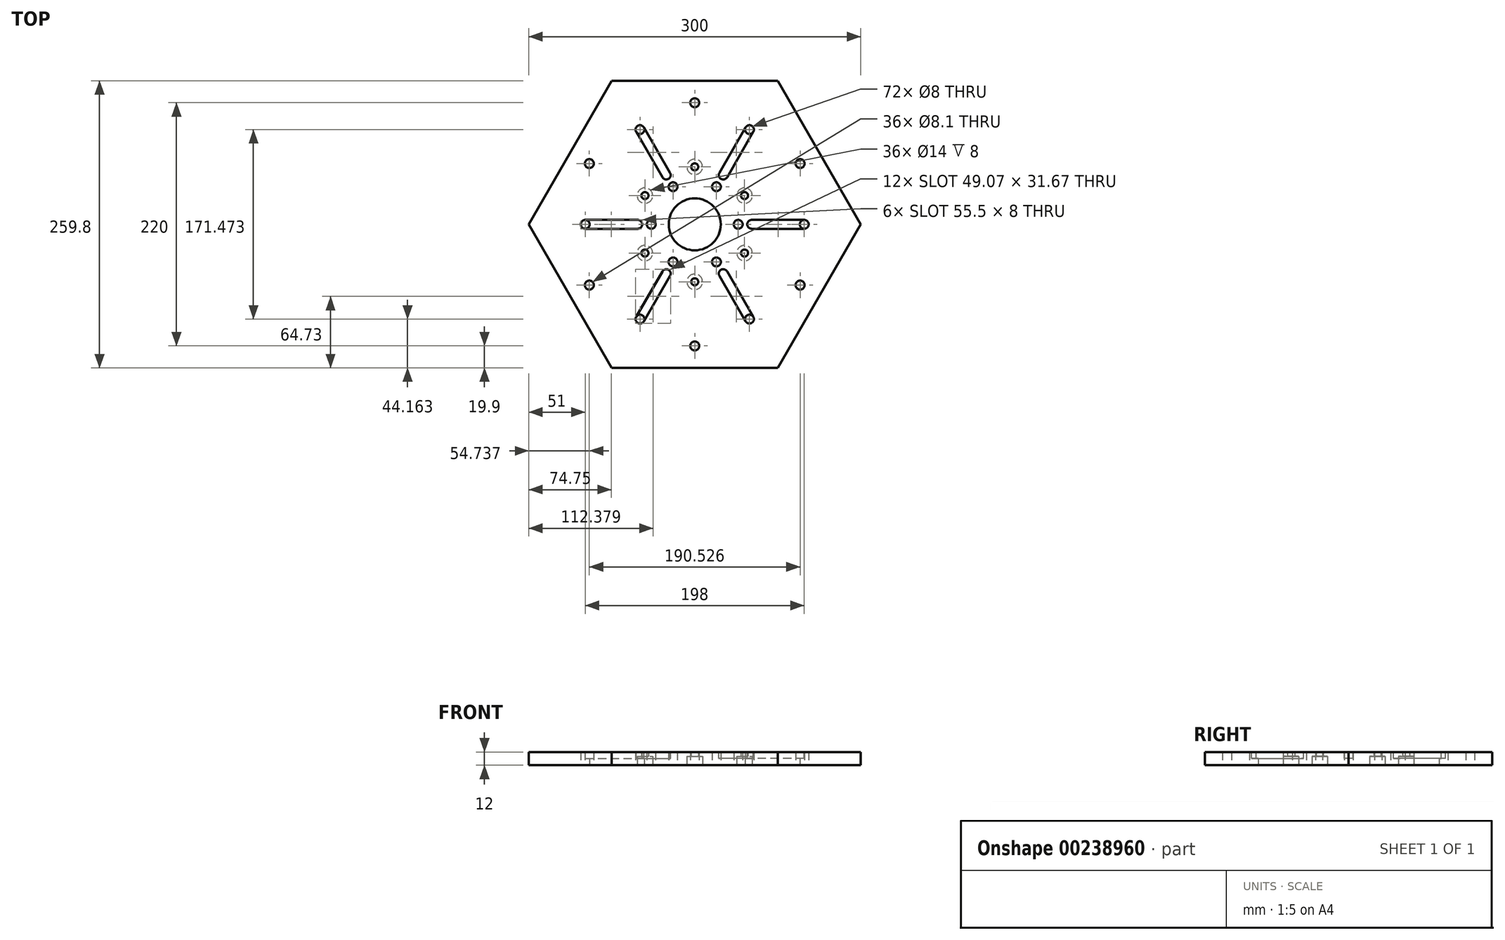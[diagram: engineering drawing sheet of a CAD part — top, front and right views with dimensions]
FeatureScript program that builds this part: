
annotation { "Feature Type Name" : "Feature", "Feature Type Description" : "" }
export const myFeature = defineFeature(function(context is Context, id is Id, definition is map)
    precondition{}
    {
        {
            var Q0;
            Q0=qCreatedBy(makeId("Top.planeOp"),FACE);
            var sketch = newSketch(context, id + "F0", { "sketchPlane" : qUnion([Q0])});
            skCircle(sketch, "E0.cCircle", {"center": v(0, 0) * mm, "radius": 150 * mm, "construction": true});
            skLineSegment(sketch, "E0.0", {"start": v(-150, 0) * mm, "end": v(-75, 129.9) * mm});
            skLineSegment(sketch, "E0.1", {"start": v(-75, 129.9) * mm, "end": v(75, 129.9) * mm});
            skLineSegment(sketch, "E0.2", {"start": v(75, 129.9) * mm, "end": v(150, 0) * mm});
            skLineSegment(sketch, "E0.3", {"start": v(150, 0) * mm, "end": v(75, -129.9) * mm});
            skLineSegment(sketch, "E0.4", {"start": v(75, -129.9) * mm, "end": v(-75, -129.9) * mm});
            skLineSegment(sketch, "E0.5", {"start": v(-75, -129.9) * mm, "end": v(-150, 0) * mm});
            skLineSegment(sketch, "E1", {"start": v(-125.66, 72.55) * mm, "end": v(0, 0) * mm, "construction": true});
            skLineSegment(sketch, "E2", {"start": v(-114.43, 89.16) * mm, "end": v(24.62, 8.88) * mm, "construction": true});
            skCircle(sketch, "E3", {"center": v(0, 0) * mm, "radius": 110 * mm, "construction": true});
            skLineSegment(sketch, "E4", {"start": v(-120.9, 10.58) * mm, "end": v(-58.23, 119.14) * mm, "construction": true});
            skCircle(sketch, "E5", {"center": v(0, 0) * mm, "radius": 95 * mm, "construction": true});
            skCircle(sketch, "E6", {"center": v(0, 0) * mm, "radius": 99 * mm, "construction": true});
            skLineSegment(sketch, "E7", {"start": v(-49.5, 85.74) * mm, "end": v(0, 0) * mm, "construction": true});
            skCircle(sketch, "E8", {"center": v(-49.5, 85.74) * mm, "radius": 4 * mm});
            skCircle(sketch, "E9", {"center": v(0, 0) * mm, "radius": 12 * mm});
            skCircle(sketch, "E10.1.0", {"center": v(-99, 0) * mm, "radius": 4 * mm});
            skCircle(sketch, "E10.2.0", {"center": v(-49.5, -85.74) * mm, "radius": 4 * mm});
            skCircle(sketch, "E10.3.0", {"center": v(49.5, -85.74) * mm, "radius": 4 * mm});
            skCircle(sketch, "E10.4.0", {"center": v(99, 0) * mm, "radius": 4 * mm});
            skCircle(sketch, "E10.5.0", {"center": v(49.5, 85.74) * mm, "radius": 4 * mm});
            skCircle(sketch, "E11", {"center": v(-85.26, 72.32) * mm, "radius": 65 * mm, "construction": true});
            skCircle(sketch, "E12", {"center": v(0, 0) * mm, "radius": 39.3 * mm, "construction": true});
            skCircle(sketch, "E13", {"center": v(-19.65, 34.03) * mm, "radius": 4 * mm});
            skCircle(sketch, "E14.1.0", {"center": v(-39.3, 0) * mm, "radius": 4 * mm});
            skCircle(sketch, "E14.2.0", {"center": v(-19.65, -34.03) * mm, "radius": 4 * mm});
            skCircle(sketch, "E14.3.0", {"center": v(19.65, -34.03) * mm, "radius": 4 * mm});
            skCircle(sketch, "E14.4.0", {"center": v(39.3, 0) * mm, "radius": 4 * mm});
            skCircle(sketch, "E14.5.0", {"center": v(19.65, 34.03) * mm, "radius": 4 * mm});
            skCircle(sketch, "E15", {"center": v(0, 110) * mm, "radius": 4.05 * mm});
            skCircle(sketch, "E16.1.0", {"center": v(-95.26, 55) * mm, "radius": 4.05 * mm});
            skCircle(sketch, "E16.2.0", {"center": v(-95.26, -55) * mm, "radius": 4.05 * mm});
            skCircle(sketch, "E16.3.0", {"center": v(0, -110) * mm, "radius": 4.05 * mm});
            skCircle(sketch, "E16.4.0", {"center": v(95.26, -55) * mm, "radius": 4.05 * mm});
            skCircle(sketch, "E16.5.0", {"center": v(95.26, 55) * mm, "radius": 4.05 * mm});
            skSolve(sketch);
        }
        {
            var Q0;
            Q0=makeQuery(id+"F0.imprint","IMPRINT",FACE,{"disambiguationData":[TD([[makeQuery(id+"F0.imprint","IMPRINT",EDGE,{"derivedFrom":sQuery(id+"F0.wireOp",EDGE,"E0.0")}),-1.0]])]});
            extrude(context, id + "F1", {"entities" : qUnion([Q0]), "depth" : 12 * mm});
        }
        {
            var Q0;
            Q0=makeQuery(id+"F0.imprint","IMPRINT",FACE,{"disambiguationData":[TD([[makeQuery(id+"F0.imprint","IMPRINT",EDGE,{"derivedFrom":sQuery(id+"F0.wireOp",EDGE,"E0.0")}),-1.0]])]});
            var sketch = newSketch(context, id + "F2", { "sketchPlane" : qUnion([Q0])});
            skCircle(sketch, "E17", {"center": v(0, 0) * mm, "radius": 23.5 * mm});
            skSolve(sketch);
        }
        {
            var Q0;
            Q0=qSketchRegion(id+"F2",true);
            extrude(context, id + "F3", {"entities" : qUnion([Q0]), "operationType" : NewBodyOperationType.REMOVE, "depth" : 12 * mm});
        }
        {
            var Q0;
            Q0=makeQuery(id+"F1.opExtrude","CAP_FACE",FACE,{"disambiguationData":[OSD([sQuery(id+"F0.wireOp",EDGE,"E0.0"),sQuery(id+"F0.wireOp",EDGE,"E0.1"),sQuery(id+"F0.wireOp",EDGE,"E0.2"),sQuery(id+"F0.wireOp",EDGE,"E0.3"),sQuery(id+"F0.wireOp",EDGE,"E0.4"),sQuery(id+"F0.wireOp",EDGE,"E0.5"),sQuery(id+"F0.wireOp",EDGE,"E8"),sQuery(id+"F0.wireOp",EDGE,"E9"),sQuery(id+"F0.wireOp",EDGE,"E10.1.0"),sQuery(id+"F0.wireOp",EDGE,"E10.2.0"),sQuery(id+"F0.wireOp",EDGE,"E10.3.0"),sQuery(id+"F0.wireOp",EDGE,"E10.4.0"),sQuery(id+"F0.wireOp",EDGE,"E10.5.0")])],"isStart":false});
            var sketch = newSketch(context, id + "F4", { "sketchPlane" : qUnion([Q0])});
            skLineSegment(sketch, "E18.0", {"start": v(-150, 0) * mm, "end": v(-75, 129.9) * mm});
            skLineSegment(sketch, "E19.0", {"start": v(-58.58, 101.47) * mm, "end": v(0, 0) * mm, "construction": true});
            skArc(sketch, "E20", {"start": v(-46, 87.67) * mm, "mid": v(-51.5, 89.2) * mm, "end": v(-52.92, 83.67) * mm});
            skLineSegment(sketch, "E21", {"start": v(-52.92, 83.67) * mm, "end": v(-29.21, 42.6) * mm});
            skLineSegment(sketch, "E22.MirrorCS", {"start": v(-46, 87.67) * mm, "end": v(-22.29, 46.6) * mm});
            skPoint(sketch, "E23.center", {"position": v(0, 0) * mm});
            skCircle(sketch, "E24", {"center": v(0, 0) * mm, "radius": 51.5 * mm, "construction": true});
            skCircle(sketch, "E25", {"center": v(0, 0) * mm, "radius": 99 * mm, "construction": true});
            skArc(sketch, "E26", {"start": v(-29.21, 42.6) * mm, "mid": v(-23.75, 41.14) * mm, "end": v(-22.29, 46.6) * mm});
            skSolve(sketch);
        }
        {
            var Q0;
            Q0=qSketchRegion(id+"F4",true);
            extrude(context, id + "F5", {"entities" : qUnion([Q0]), "oppositeDirection" : true, "depth" : 6 * mm, "hasSecondDirection" : true, "secondDirectionOppositeDirection" : false, "secondDirectionDepth" : 10 * mm});
        }
        {
            var Q0;
            Q0=makeQuery(id+"F5.opExtrude","SWEPT_BODY",BODY,{"disambiguationData":[OSD([sQuery(id+"F4.wireOp",EDGE,"E20"),sQuery(id+"F4.wireOp",EDGE,"E21"),sQuery(id+"F4.wireOp",EDGE,"E22.MirrorCS"),sQuery(id+"F4.wireOp",EDGE,"CpuIoytq-DRnW-63yL-89Dn-rdrzzWqcRoiw")])]});
            var Q1;
            Q1=makeQuery(id+"F3.boolean.opBoolean","COPY",FACE,{"derivedFrom":makeQuery(id+"F3.opExtrude","SWEPT_FACE",FACE,{"disambiguationData":[OSD([sQuery(id+"F2.wireOp",EDGE,"E17")])]})});
            circularPattern(context, id + "F6", {"operationType" : NewBodyOperationType.REMOVE, "entities" : qUnion([Q0]), "axis" : qUnion([Q1]), "angle" : 360 * degree, "instanceCount" : 6, "equalSpace" : true});
        }
        {
            var Q0;
            Q0=makeQuery(id+"F1.opExtrude","CAP_FACE",FACE,{"disambiguationData":[OSD([sQuery(id+"F0.wireOp",EDGE,"E0.0"),sQuery(id+"F0.wireOp",EDGE,"E0.1"),sQuery(id+"F0.wireOp",EDGE,"E0.2"),sQuery(id+"F0.wireOp",EDGE,"E0.3"),sQuery(id+"F0.wireOp",EDGE,"E0.4"),sQuery(id+"F0.wireOp",EDGE,"E0.5"),sQuery(id+"F0.wireOp",EDGE,"E8"),sQuery(id+"F0.wireOp",EDGE,"E9"),sQuery(id+"F0.wireOp",EDGE,"E10.1.0"),sQuery(id+"F0.wireOp",EDGE,"E10.2.0"),sQuery(id+"F0.wireOp",EDGE,"E10.3.0"),sQuery(id+"F0.wireOp",EDGE,"E10.4.0"),sQuery(id+"F0.wireOp",EDGE,"E10.5.0"),sQuery(id+"F0.wireOp",EDGE,"E13"),sQuery(id+"F0.wireOp",EDGE,"E14.1.0"),sQuery(id+"F0.wireOp",EDGE,"E14.2.0"),sQuery(id+"F0.wireOp",EDGE,"E14.3.0"),sQuery(id+"F0.wireOp",EDGE,"E14.4.0"),sQuery(id+"F0.wireOp",EDGE,"E14.5.0"),sQuery(id+"F0.wireOp",EDGE,"E15"),sQuery(id+"F0.wireOp",EDGE,"E16.1.0"),sQuery(id+"F0.wireOp",EDGE,"E16.2.0"),sQuery(id+"F0.wireOp",EDGE,"E16.3.0"),sQuery(id+"F0.wireOp",EDGE,"E16.4.0"),sQuery(id+"F0.wireOp",EDGE,"E16.5.0")])],"isStart":true});
            var sketch = newSketch(context, id + "F7", { "sketchPlane" : qUnion([Q0])});
            skLineSegment(sketch, "E27", {"start": v(0, 0) * mm, "end": v(0, 69.38) * mm, "construction": true});
            skCircle(sketch, "E28", {"center": v(0, 0) * mm, "radius": 52 * mm, "construction": true});
            skPoint(sketch, "E29", {"position": v(0, 52) * mm});
            skPoint(sketch, "E30.1.0", {"position": v(-45.03, 26) * mm});
            skPoint(sketch, "E30.2.0", {"position": v(-45.03, -26) * mm});
            skPoint(sketch, "E31.0.3.0", {"position": v(0, -52) * mm});
            skPoint(sketch, "E31.0.4.0", {"position": v(45.03, -26) * mm});
            skPoint(sketch, "E31.0.5.0", {"position": v(45.03, 26) * mm});
            skSolve(sketch);
        }
        {
            var Q0;
            Q0=sQuery(id+"F7.wireOp",VERTEX,"E29");
            var Q1;
            Q1=sQuery(id+"F7.wireOp",VERTEX,"E30.1.0");
            var Q2;
            Q2=sQuery(id+"F7.wireOp",VERTEX,"E30.2.0");
            var Q3;
            Q3=sQuery(id+"F7.wireOp",VERTEX,"E31.0.3.0");
            var Q4;
            Q4=sQuery(id+"F7.wireOp",VERTEX,"E31.0.4.0");
            var Q5;
            Q5=sQuery(id+"F7.wireOp",VERTEX,"E31.0.5.0");
            var Q6;
            Q6=makeQuery(id+"F1.opExtrude","SWEPT_BODY",BODY,{"disambiguationData":[OSD([sQuery(id+"F0.wireOp",EDGE,"E0.0"),sQuery(id+"F0.wireOp",EDGE,"E0.1"),sQuery(id+"F0.wireOp",EDGE,"E0.2"),sQuery(id+"F0.wireOp",EDGE,"E0.3"),sQuery(id+"F0.wireOp",EDGE,"E0.4"),sQuery(id+"F0.wireOp",EDGE,"E0.5"),sQuery(id+"F0.wireOp",EDGE,"E8"),sQuery(id+"F0.wireOp",EDGE,"E9"),sQuery(id+"F0.wireOp",EDGE,"E10.1.0"),sQuery(id+"F0.wireOp",EDGE,"E10.2.0"),sQuery(id+"F0.wireOp",EDGE,"E10.3.0"),sQuery(id+"F0.wireOp",EDGE,"E10.4.0"),sQuery(id+"F0.wireOp",EDGE,"E10.5.0"),sQuery(id+"F0.wireOp",EDGE,"E13"),sQuery(id+"F0.wireOp",EDGE,"E14.1.0"),sQuery(id+"F0.wireOp",EDGE,"E14.2.0"),sQuery(id+"F0.wireOp",EDGE,"E14.3.0"),sQuery(id+"F0.wireOp",EDGE,"E14.4.0"),sQuery(id+"F0.wireOp",EDGE,"E14.5.0"),sQuery(id+"F0.wireOp",EDGE,"E15"),sQuery(id+"F0.wireOp",EDGE,"E16.1.0"),sQuery(id+"F0.wireOp",EDGE,"E16.2.0"),sQuery(id+"F0.wireOp",EDGE,"E16.3.0"),sQuery(id+"F0.wireOp",EDGE,"E16.4.0"),sQuery(id+"F0.wireOp",EDGE,"E16.5.0")])]});
            hole(context, id + "F8", {"style" : HoleStyle.C_BORE, "endStyle" : HoleEndStyle.BLIND, "holeDiameter" : 6.4 * mm, "cBoreDiameter" : 14 * mm, "cBoreDepth" : 8 * mm, "holeDepth" : 20 * mm, "locations" : qUnion([Q0, Q1, Q2, Q3, Q4, Q5]), "scope" : qUnion([Q6])});
        }
    });
